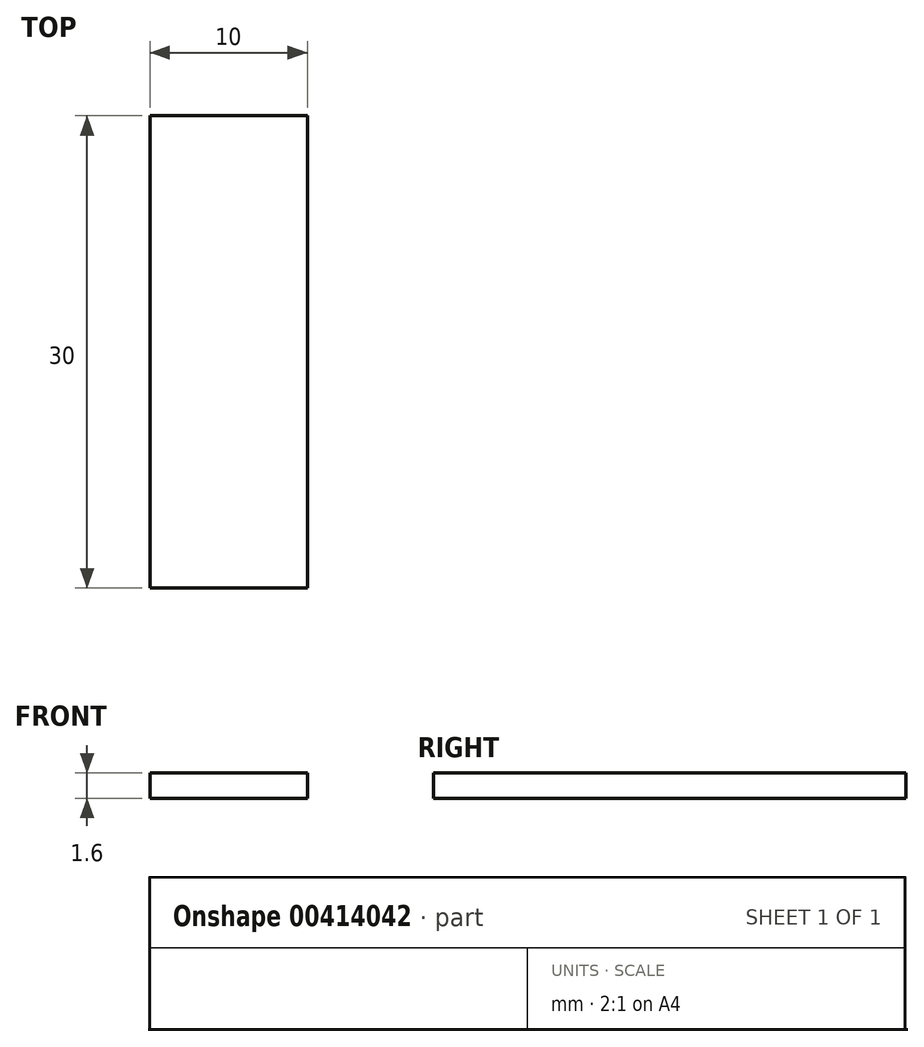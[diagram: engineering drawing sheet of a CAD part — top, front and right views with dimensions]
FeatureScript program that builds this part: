
annotation { "Feature Type Name" : "Feature", "Feature Type Description" : "" }
export const myFeature = defineFeature(function(context is Context, id is Id, definition is map)
    precondition{}
    {
        {
            var Q0;
            Q0=qCreatedBy(makeId("Top.planeOp"),FACE);
            var sketch = newSketch(context, id + "F0", { "sketchPlane" : qUnion([Q0])});
            skLineSegment(sketch, "E0.bottom", {"start": v(0.59, 18.92) * mm, "end": v(10.59, 18.92) * mm});
            skLineSegment(sketch, "E0.top", {"start": v(0.59, -11.08) * mm, "end": v(10.59, -11.08) * mm});
            skLineSegment(sketch, "E0.left", {"start": v(0.59, 18.92) * mm, "end": v(0.59, -11.08) * mm});
            skLineSegment(sketch, "E0.right", {"start": v(10.59, 18.92) * mm, "end": v(10.59, -11.08) * mm});
            skSolve(sketch);
        }
        {
            var Q0;
            Q0 = qSketchRegion(id + "F0", true);
            extrude(context, id + "F1", {"entities" : qUnion([Q0]), "depth" : 1.6 * mm});
        }
    });
